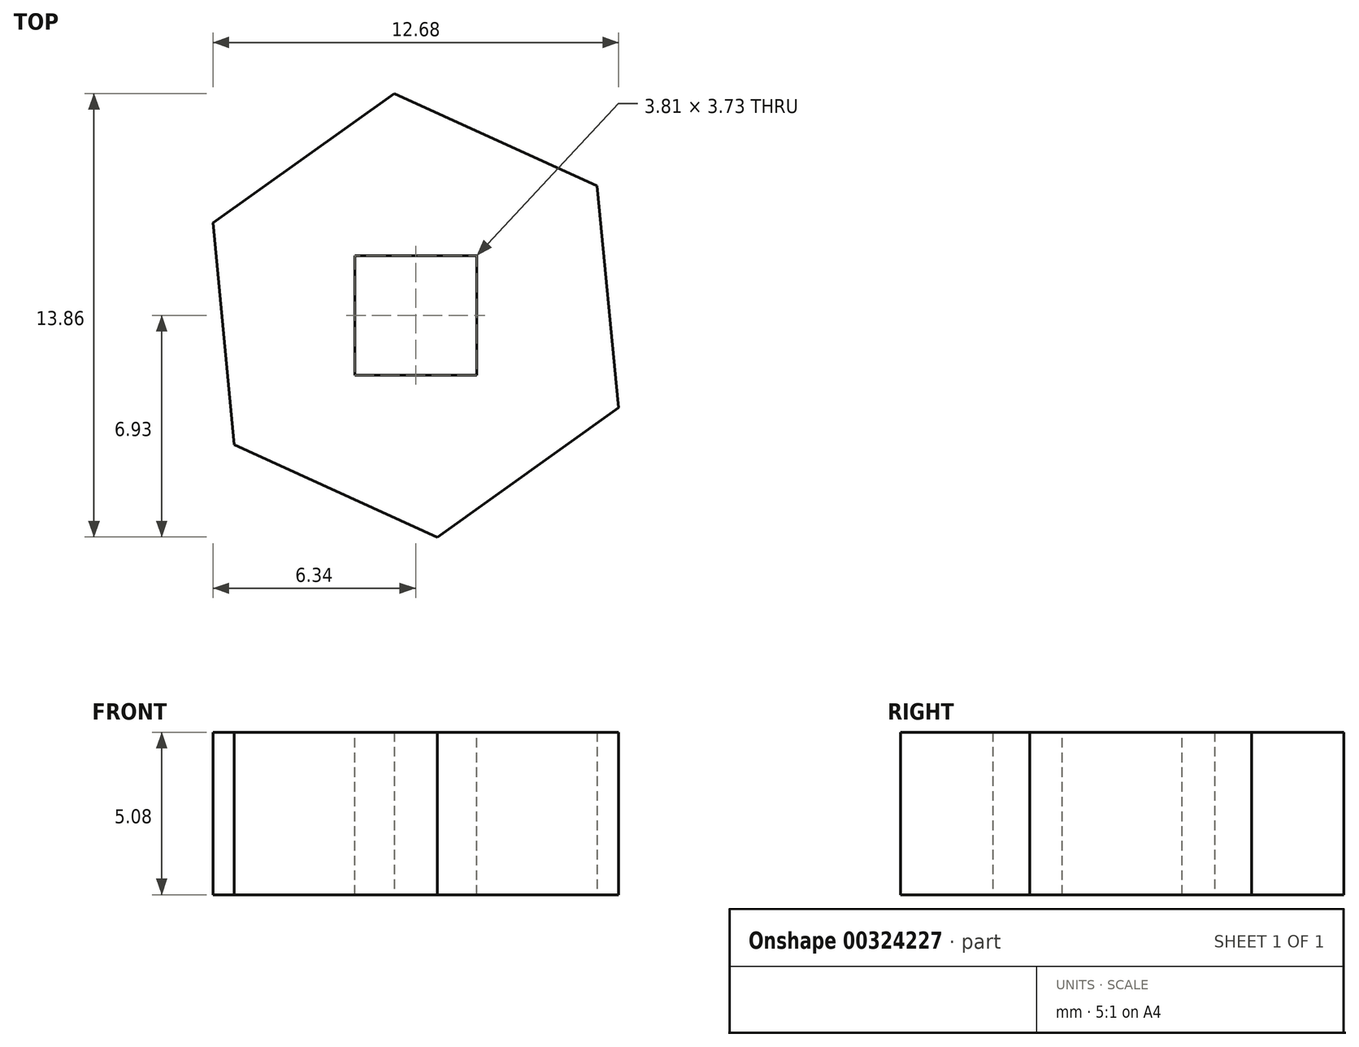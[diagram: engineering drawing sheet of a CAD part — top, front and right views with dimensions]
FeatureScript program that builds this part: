
annotation { "Feature Type Name" : "Feature", "Feature Type Description" : "" }
export const myFeature = defineFeature(function(context is Context, id is Id, definition is map)
    precondition{}
    {
        {
            var Q0;
            Q0=qCreatedBy(makeId("Top.planeOp"),FACE);
            var sketch = newSketch(context, id + "F0", { "sketchPlane" : qUnion([Q0])});
            skCircle(sketch, "E0.cCircle", {"center": v(0, 0) * mm, "radius": 6.03 * mm, "construction": true});
            skLineSegment(sketch, "E0.0", {"start": v(6.34, -2.89) * mm, "end": v(0.67, -6.93) * mm});
            skLineSegment(sketch, "E0.1", {"start": v(0.67, -6.93) * mm, "end": v(-5.67, -4.05) * mm});
            skLineSegment(sketch, "E0.2", {"start": v(-5.67, -4.05) * mm, "end": v(-6.34, 2.89) * mm});
            skLineSegment(sketch, "E0.3", {"start": v(-6.34, 2.89) * mm, "end": v(-0.67, 6.93) * mm});
            skLineSegment(sketch, "E0.4", {"start": v(-0.67, 6.93) * mm, "end": v(5.67, 4.05) * mm});
            skLineSegment(sketch, "E0.5", {"start": v(5.67, 4.05) * mm, "end": v(6.34, -2.89) * mm});
            skPoint(sketch, "E0.0.midPoint", {"position": v(3.5, -4.9) * mm});
            skSolve(sketch);
        }
        {
            var Q0;
            Q0 = qSketchRegion(id + "F0", true);
            extrude(context, id + "F1", {"entities" : qUnion([Q0]), "depth" : 5.08 * mm});
        }
        {
            var Q0;
            Q0=makeQuery(id+"F1.opExtrude","CAP_FACE",FACE,{"disambiguationData":[OSD([sQuery(id+"F0.wireOp",EDGE,"E0.0"),sQuery(id+"F0.wireOp",EDGE,"E0.1"),sQuery(id+"F0.wireOp",EDGE,"E0.2"),sQuery(id+"F0.wireOp",EDGE,"E0.3"),sQuery(id+"F0.wireOp",EDGE,"E0.4"),sQuery(id+"F0.wireOp",EDGE,"E0.5")])],"isStart":false});
            var sketch = newSketch(context, id + "F2", { "sketchPlane" : qUnion([Q0])});
            skLineSegment(sketch, "E1.bottom", {"start": v(1.9, 1.87) * mm, "end": v(-1.9, 1.87) * mm});
            skLineSegment(sketch, "E1.top", {"start": v(1.9, -1.87) * mm, "end": v(-1.9, -1.87) * mm});
            skLineSegment(sketch, "E1.left", {"start": v(1.9, 1.87) * mm, "end": v(1.9, -1.87) * mm});
            skLineSegment(sketch, "E1.right", {"start": v(-1.9, 1.87) * mm, "end": v(-1.9, -1.87) * mm});
            skPoint(sketch, "E1.middle", {"position": v(0, 0) * mm});
            skSolve(sketch);
        }
        {
            var Q0;
            Q0 = qSketchRegion(id + "F2", true);
            extrude(context, id + "F3", {"entities" : qUnion([Q0]), "operationType" : NewBodyOperationType.REMOVE, "oppositeDirection" : true, "depth" : 25.4 * mm});
        }
    });
